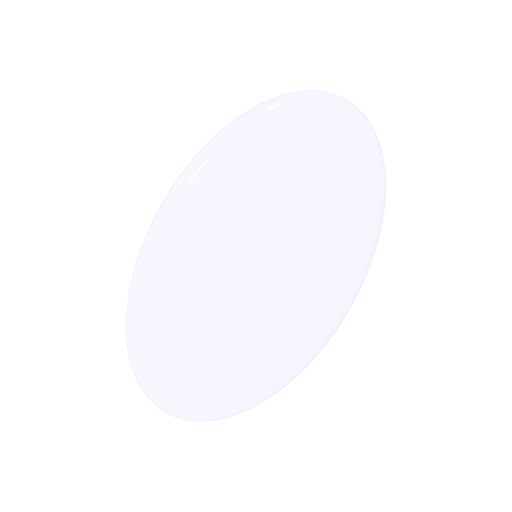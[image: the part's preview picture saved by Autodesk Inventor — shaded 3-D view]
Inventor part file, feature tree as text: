
AUTODESK INVENTOR PART (.ipt)
format: ipt  version: 2023 (Build 270158000, 158)  size: 157,696 bytes
history: native  units: in
note: dims shown in document units (in); Inventor stores cm internally (conversion verified against a paired STEP export)
features: revolve x1, sketch x1
ambient origin geometry x8: Origin, YZ Plane, XZ Plane, XY Plane, X Axis, Y Axis, Z Axis, Center Point
bodies: Solid1 (feature_tree)
feature tree (2):
  revolve  "Revolution1"  [1 undecoded]
  sketch  "Sketch1"  dims[d0=7.874in d1=43.3071in d2=90.0deg]
note: 1 required parameter value undecoded (feature->parameter linkage not recoverable at this tier; creation-order binding heuristic only, values carry confidence <= 0.55)
